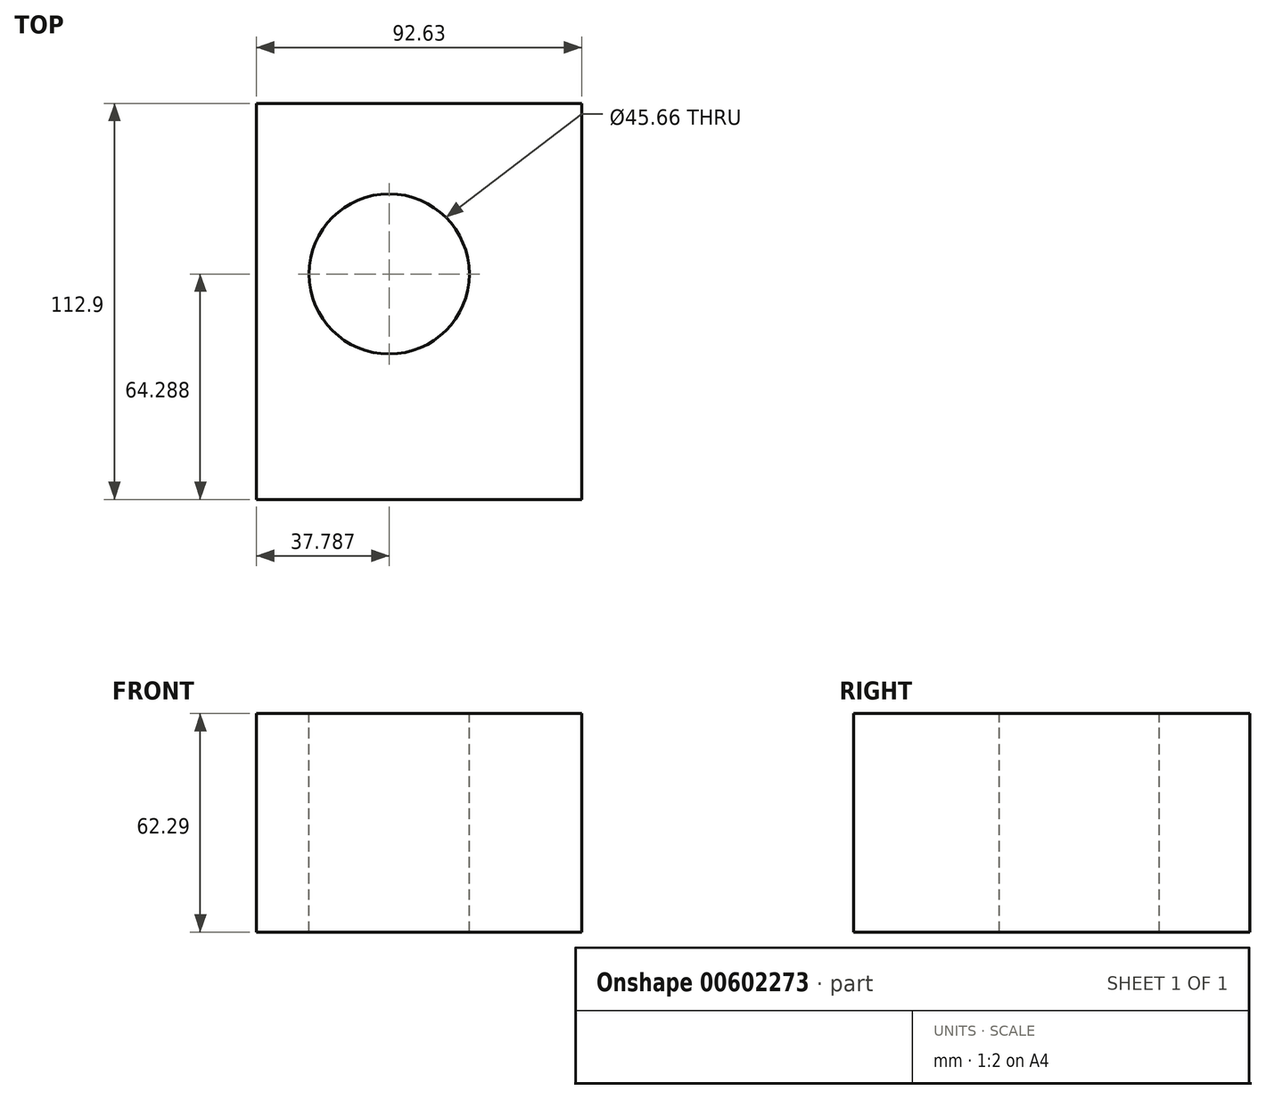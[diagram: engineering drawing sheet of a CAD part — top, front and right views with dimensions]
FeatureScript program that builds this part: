
annotation { "Feature Type Name" : "Feature", "Feature Type Description" : "" }
export const myFeature = defineFeature(function(context is Context, id is Id, definition is map)
    precondition{}
    {
        {
            var Q0;
            Q0=qCreatedBy(makeId("Front.planeOp"),FACE);
            var sketch = newSketch(context, id + "F0", { "sketchPlane" : qUnion([Q0])});
            skLineSegment(sketch, "E0.bottom", {"start": v(0, 0) * mm, "end": v(92.63, 0) * mm});
            skLineSegment(sketch, "E0.top", {"start": v(0, 62.29) * mm, "end": v(92.63, 62.29) * mm});
            skLineSegment(sketch, "E0.left", {"start": v(0, 0) * mm, "end": v(0, 62.29) * mm});
            skLineSegment(sketch, "E0.right", {"start": v(92.63, 0) * mm, "end": v(92.63, 62.29) * mm});
            skSolve(sketch);
        }
        {
            var Q0;
            Q0=makeQuery(id+"F0.imprint","IMPRINT",FACE,{"disambiguationData":[TD([[makeQuery(id+"F0.imprint","IMPRINT",EDGE,{"derivedFrom":sQuery(id+"F0.wireOp",EDGE,"E0.bottom")}),1.0]])]});
            extrude(context, id + "F1", {"entities" : qUnion([Q0]), "depth" : 112.9 * mm, "offsetDistance" : 25 * mm});
        }
        {
            var Q0;
            Q0=makeQuery(id+"F1.opExtrude","SWEPT_FACE",FACE,{"disambiguationData":[OSD([sQuery(id+"F0.wireOp",EDGE,"E0.top")])]});
            var sketch = newSketch(context, id + "F2", { "sketchPlane" : qUnion([Q0])});
            skCircle(sketch, "E1", {"center": v(37.79, -48.61) * mm, "radius": 22.83 * mm});
            skSolve(sketch);
        }
        {
            var Q0;
            Q0=makeQuery(id+"F2.imprint","IMPRINT",FACE,{"disambiguationData":[TD([[makeQuery(id+"F2.imprint","IMPRINT",EDGE,{"derivedFrom":sQuery(id+"F2.wireOp",EDGE,"E1")}),1.0]])]});
            extrude(context, id + "F3", {"entities" : qUnion([Q0]), "operationType" : NewBodyOperationType.REMOVE, "oppositeDirection" : true, "depth" : 124.5 * mm, "offsetDistance" : 25 * mm});
        }
    });
